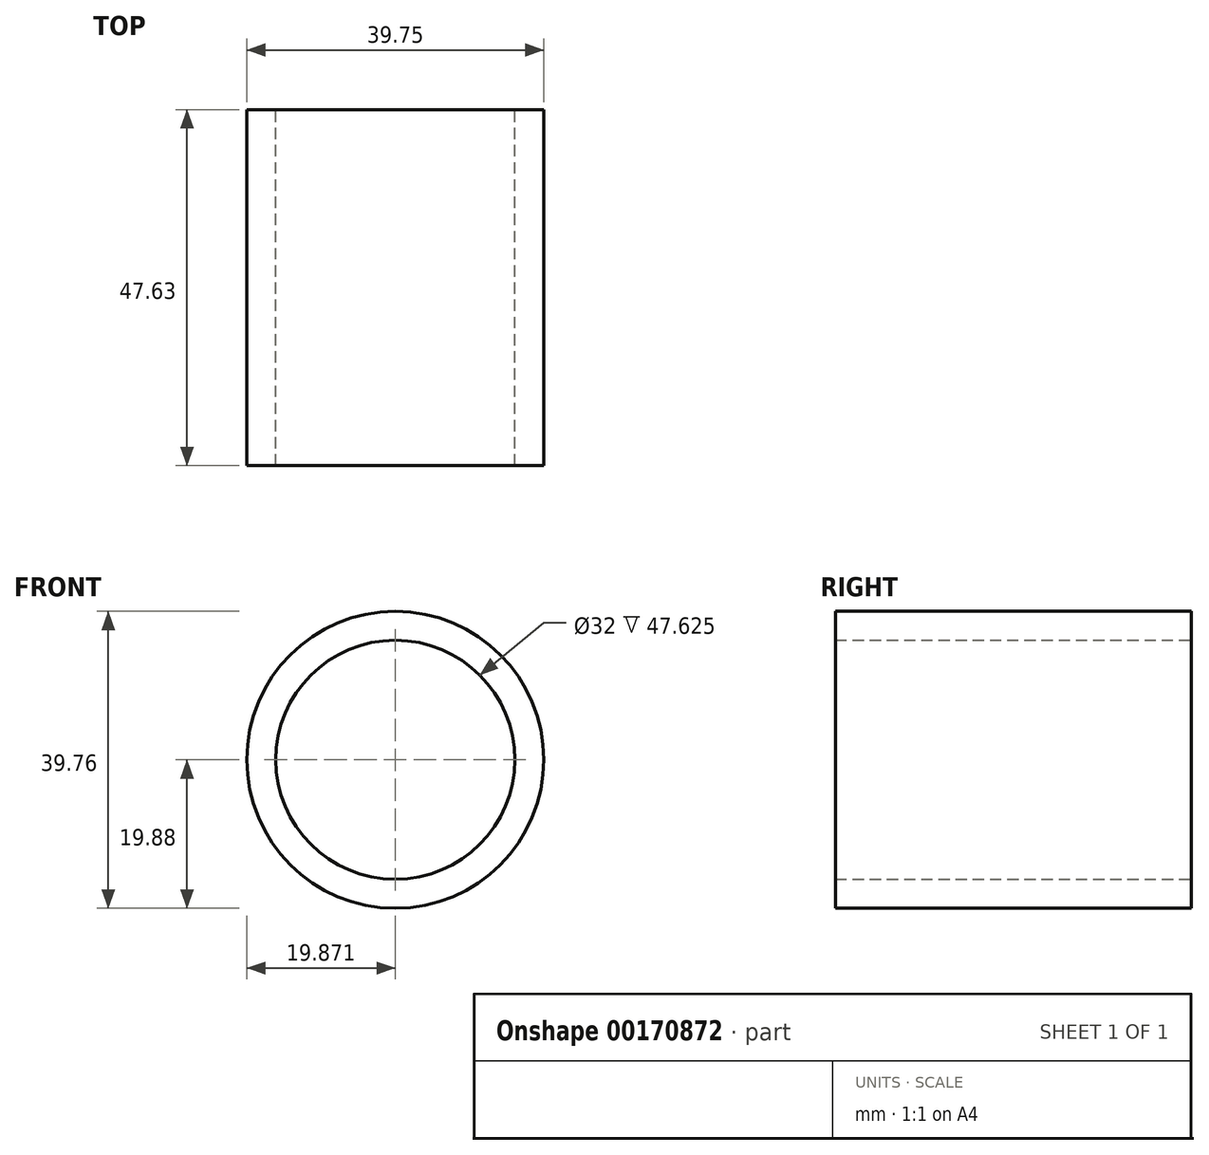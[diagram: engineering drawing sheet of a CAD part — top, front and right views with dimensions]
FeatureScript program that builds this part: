
annotation { "Feature Type Name" : "Feature", "Feature Type Description" : "" }
export const myFeature = defineFeature(function(context is Context, id is Id, definition is map)
    precondition{}
    {
        {
            var Q0;
            Q0=qCreatedBy(makeId("Front.planeOp"),FACE);
            var sketch = newSketch(context, id + "F0", { "sketchPlane" : qUnion([Q0])});
            skCircle(sketch, "E0", {"center": v(-1.8, 0) * mm, "radius": 16 * mm});
            skCircle(sketch, "E1", {"center": v(-1.8, 0) * mm, "radius": 19.88 * mm});
            skSolve(sketch);
        }
        {
            var Q0;
            Q0 = qSketchRegion(id + "F0", true);
            extrude(context, id + "F1", {"entities" : qUnion([Q0]), "depth" : 47.62 * mm});
        }
    });
